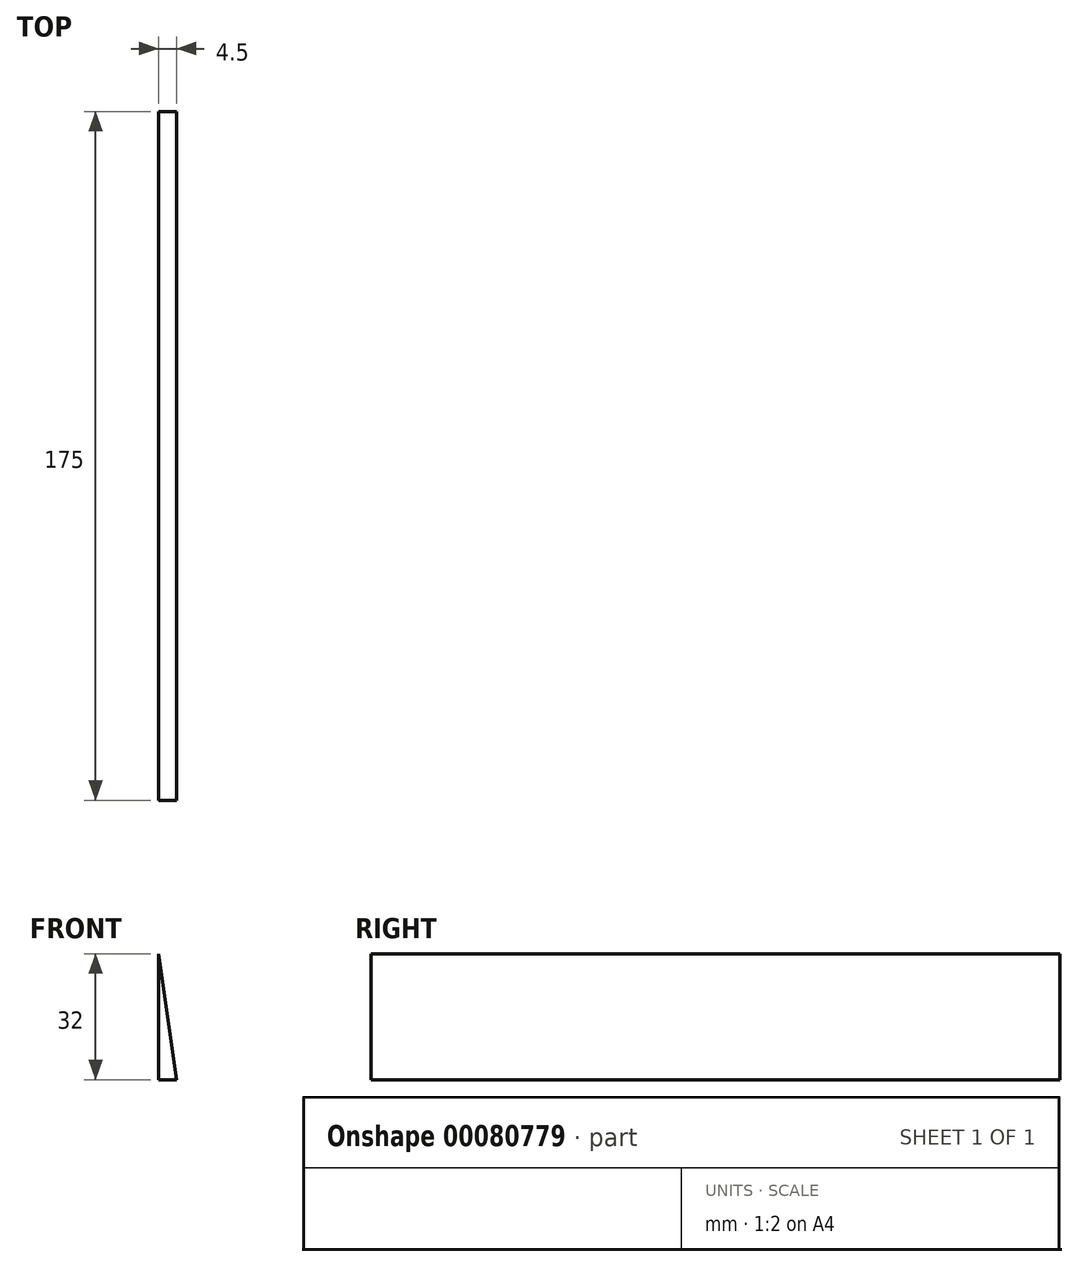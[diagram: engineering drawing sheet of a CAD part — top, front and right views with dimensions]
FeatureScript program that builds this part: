
annotation { "Feature Type Name" : "Feature", "Feature Type Description" : "" }
export const myFeature = defineFeature(function(context is Context, id is Id, definition is map)
    precondition{}
    {
        {
            var Q0;
            Q0=qCreatedBy(makeId("Front.planeOp"),FACE);
            var sketch = newSketch(context, id + "F0", { "sketchPlane" : qUnion([Q0])});
            skLineSegment(sketch, "E0", {"start": v(0, 0) * mm, "end": v(4.5, 0) * mm});
            skLineSegment(sketch, "E1", {"start": v(4.5, 0) * mm, "end": v(0, 32) * mm});
            skLineSegment(sketch, "E2", {"start": v(0, 32) * mm, "end": v(0, 0) * mm});
            skSolve(sketch);
        }
        {
            var Q0;
            Q0=makeQuery(id+"F0.imprint","IMPRINT",FACE,{"disambiguationData":[TD([[makeQuery(id+"F0.imprint","IMPRINT",EDGE,{"derivedFrom":sQuery(id+"F0.wireOp",EDGE,"E0")}),1.0]])]});
            extrude(context, id + "F1", {"entities" : qUnion([Q0]), "depth" : 175 * mm});
        }
    });
